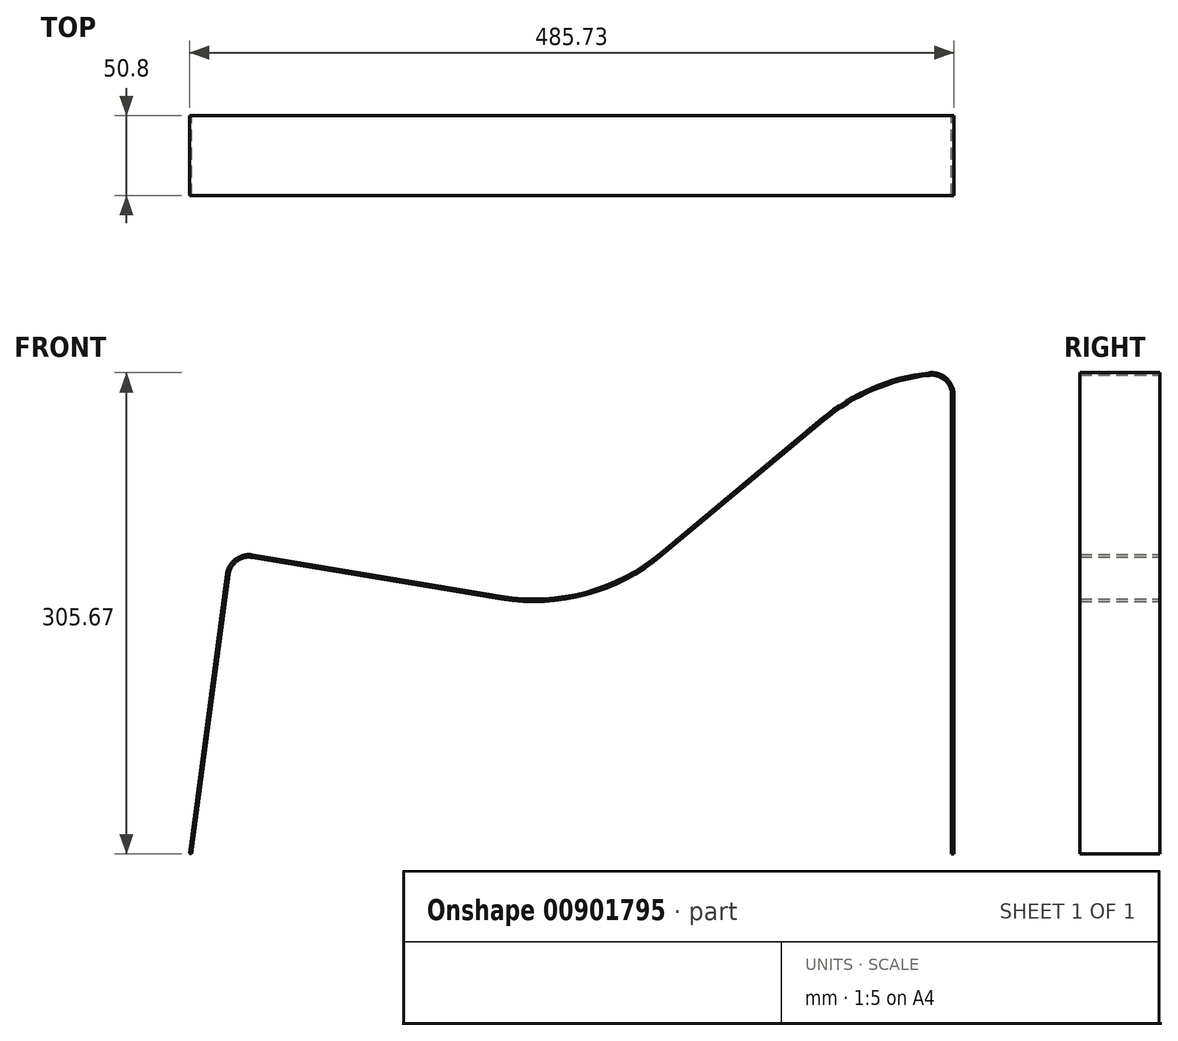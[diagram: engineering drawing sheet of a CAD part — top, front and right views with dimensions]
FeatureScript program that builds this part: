
annotation { "Feature Type Name" : "Feature", "Feature Type Description" : "" }
export const myFeature = defineFeature(function(context is Context, id is Id, definition is map)
    precondition{}
    {
        {
            var Q0;
            Q0=qCreatedBy(makeId("Front.planeOp"),FACE);
            var sketch = newSketch(context, id + "F0", { "sketchPlane" : qUnion([Q0])});
            skLineSegment(sketch, "E0", {"start": v(0, 0) * mm, "end": v(23.67, 177.5) * mm});
            skLineSegment(sketch, "E1", {"start": v(38.34, 188.34) * mm, "end": v(196.5, 161.98) * mm});
            skLineSegment(sketch, "E2", {"start": v(298.76, 189.76) * mm, "end": v(401.21, 275.3) * mm});
            skLineSegment(sketch, "E3", {"start": v(482.6, 291.4) * mm, "end": v(482.6, 0) * mm});
            skPoint(sketch, "E4.visualSharp", {"position": v(431.85, 300.87) * mm});
            skArc(sketch, "E4.filletArc", {"start": v(468.49, 304.01) * mm, "mid": v(432.74, 294.6) * mm, "end": v(401.21, 275.3) * mm});
            skPoint(sketch, "E5.visualSharp", {"position": v(482.6, 304.8) * mm});
            skArc(sketch, "E5.filletArc", {"start": v(482.6, 291.4) * mm, "mid": v(478.37, 300.86) * mm, "end": v(468.49, 304.01) * mm});
            skPoint(sketch, "E6.visualSharp", {"position": v(254, 152.4) * mm});
            skArc(sketch, "E6.filletArc", {"start": v(196.5, 161.98) * mm, "mid": v(250.66, 164.7) * mm, "end": v(298.76, 189.76) * mm});
            skPoint(sketch, "E7.visualSharp", {"position": v(25.4, 190.5) * mm});
            skArc(sketch, "E7.filletArc", {"start": v(38.34, 188.34) * mm, "mid": v(28.7, 186.03) * mm, "end": v(23.67, 177.5) * mm});
            skLineSegment(sketch, "E8.0", {"start": v(484.17, 291.4) * mm, "end": v(484.17, 0) * mm});
            skArc(sketch, "E8.1", {"start": v(484.17, 291.4) * mm, "mid": v(479.42, 302.03) * mm, "end": v(468.31, 305.58) * mm});
            skArc(sketch, "E8.2", {"start": v(468.31, 305.58) * mm, "mid": v(432.12, 296.05) * mm, "end": v(400.2, 276.5) * mm});
            skLineSegment(sketch, "E8.3", {"start": v(297.75, 190.97) * mm, "end": v(400.2, 276.5) * mm});
            skLineSegment(sketch, "E8.4", {"start": v(-1.56, 0.2) * mm, "end": v(22.1, 177.7) * mm});
            skArc(sketch, "E8.5", {"start": v(38.6, 189.9) * mm, "mid": v(27.77, 187.3) * mm, "end": v(22.1, 177.7) * mm});
            skLineSegment(sketch, "E8.6", {"start": v(38.6, 189.9) * mm, "end": v(196.75, 163.54) * mm});
            skArc(sketch, "E8.7", {"start": v(196.75, 163.54) * mm, "mid": v(250.25, 166.22) * mm, "end": v(297.75, 190.97) * mm});
            skLineSegment(sketch, "E9", {"start": v(-1.56, 0.2) * mm, "end": v(0, 0) * mm});
            skLineSegment(sketch, "E10", {"start": v(484.17, 0) * mm, "end": v(482.6, 0) * mm});
            skSolve(sketch);
        }
        {
            var Q0;
            Q0 = qSketchRegion(id + "F0", true);
            extrude(context, id + "F1", {"entities" : qUnion([Q0]), "depth" : 25.4 * mm, "offsetDistance" : 25.4 * mm, "hasSecondDirection" : true, "secondDirectionOppositeDirection" : true, "secondDirectionDepth" : 25.4 * mm});
        }
    });
